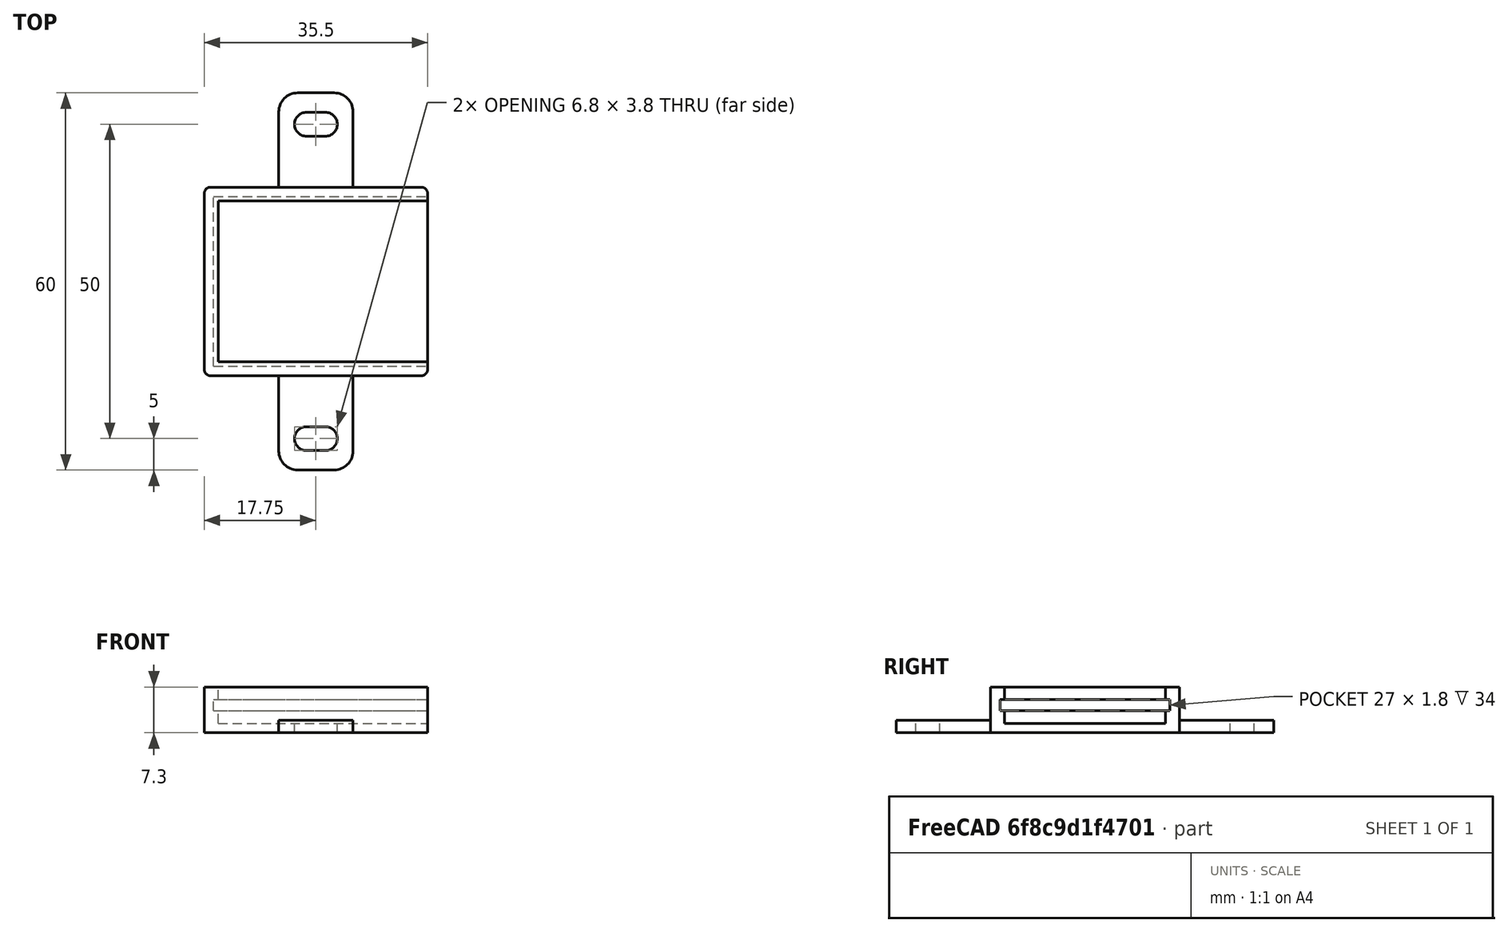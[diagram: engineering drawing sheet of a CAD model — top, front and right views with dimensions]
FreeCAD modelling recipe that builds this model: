
FCSTD DOCUMENT  (FreeCAD 0.19R)
Label: leds_27x34
License: FreeArt
LicenseURL: http://artlibre.org/licence/lal
objects: Part::Box×3, Part::MultiFuse×2, Spreadsheet::Sheet×1, Part::Fillet×1, Part::Feature×1, Part::Cut×1, App::Part×1
note: 8 computed .brp shape members not serialized (recipe doc carries the construction recipe); baked Part::Feature solids carry a one-line shape summary decoded from their .brp

FEATURE [Spreadsheet::Sheet] Spreadsheet  label="p"
  cells = A1=pcb_x; B1(pcb_x)=34; A2=pcb_y; B2(pcb_y)=27; A3=pcb_z; B3(pcb_z)=1.8; A4=pcb_under; B4(pcb_under)=2; A5=side_wall; B5(side_wall)=1.5; A6=pcb_side_lane; B6(pcb_side_lane)=0.7; A7=bottom_wall; B7(bottom_wall)=1.5; A8=pcb_above; B8(pcb_above)=2
FEATURE [Part::Box] Box  label="external cube"
  AttacherType = Attacher::AttachEngine3D
  Height = 7.3
  Length = 35.5
  Width = 30
  expr: Length = <<p>>.pcb_x + <<p>>.side_wall
  expr: Width = <<p>>.pcb_y + 2 * <<p>>.side_wall
  expr: Height = <<p>>.bottom_wall + <<p>>.pcb_under + <<p>>.pcb_z + <<p>>.pcb_above
FEATURE [Part::Box] Box006  label="internal cube"
  AttacherType = Attacher::AttachEngine3D
  Height = 5.8
  Length = 34.1
  Placement = pos=(2.2,2.2,1.5) rot=(0,0,1;0rad)
  Width = 25.6
  expr: Length = <<p>>.pcb_x - 2 * <<p>>.pcb_side_lane + <<p>>.side_wall
  expr: Width = <<p>>.pcb_y - 2 * <<p>>.pcb_side_lane
  expr: Height = <<p>>.pcb_under + <<p>>.pcb_z + <<p>>.pcb_above
  expr: .Placement.Base.z = <<p>>.bottom_wall
  expr: .Placement.Base.x = <<p>>.side_wall + <<p>>.pcb_side_lane
  expr: .Placement.Base.y = <<p>>.side_wall + <<p>>.pcb_side_lane
FEATURE [Part::Box] Box007  label="pcb extract cube"
  AttacherType = Attacher::AttachEngine3D
  Height = 1.8
  Length = 34
  Placement = pos=(1.5,1.5,3.5) rot=(0,0,1;0rad)
  Width = 27
  expr: Height = <<p>>.pcb_z
  expr: .Placement.Base.z = <<p>>.bottom_wall + <<p>>.pcb_under
  expr: Width = <<p>>.pcb_y
  expr: Length = <<p>>.pcb_x
  expr: .Placement.Base.x = <<p>>.side_wall
  expr: .Placement.Base.y = <<p>>.side_wall
FEATURE [Part::MultiFuse] Fusion  label="extract fusion"
  Shapes = -> [Box006,Box007]
FEATURE [Part::Fillet] Fillet  label="external fillet"
  Base = -> Box
  Edges = 4 edges r=1: [Edge1,Edge3,Edge5,Edge7]
FEATURE [Part::Feature] Cut002001  label="attach plane y dir001"
  Placement = pos=(11.85,-15,0) rot=(0,0,1;0rad)
  shape: bbox 11.8 x 60 x 2 mm, 20 faces (baked)
FEATURE [Part::MultiFuse] Fusion001  label="solid fusion"
  Shapes = -> [Fillet,Cut002001]
FEATURE [Part::Cut] Cut  label="body cut"
  Base = -> Fusion001
  Tool = -> Fusion
FEATURE [App::Part] Part  label="leds_8_gnd_common part"
  Group = -> [Box,Fillet,Fusion001,Fusion,Box007,Box006,Cut]
  Origin = -> Origin
